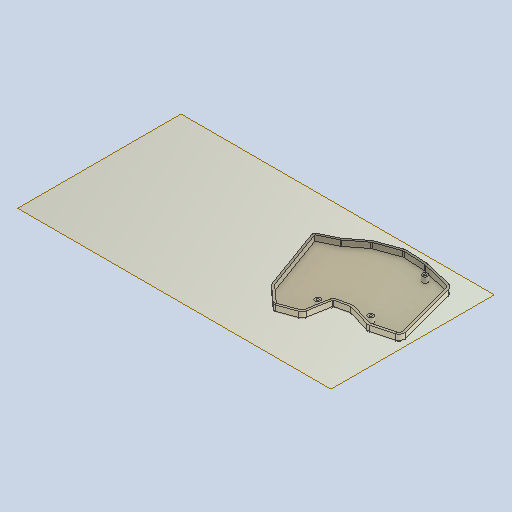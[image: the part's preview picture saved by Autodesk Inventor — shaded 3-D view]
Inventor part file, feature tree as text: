
AUTODESK INVENTOR PART (.ipt)
format: ipt  version: 2024 (Build 280153000, 153)  size: 275,456 bytes
history: native  units: mm
features: other x3, sketch x2, plane x1
ambient origin geometry x8: Origin, YZ Plane, XZ Plane, XY Plane, X Axis, Y Axis, Z Axis, Center Point
bodies: Volumenkörper1 (feature_tree)
feature tree (6):
  other  "left_bottom.ipt"
  other  "Volumenkörper1::left_bottom.ipt"
  other  "Bezeichnung1"
  sketch  "Skizze1"  dims[d0=10.0mm]
  sketch  "Skizze2"
  plane  "Arbeitsebene1"
